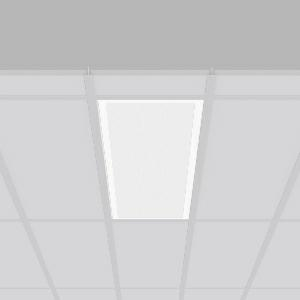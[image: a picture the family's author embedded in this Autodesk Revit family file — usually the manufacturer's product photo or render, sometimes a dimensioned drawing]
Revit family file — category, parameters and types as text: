
# Revit family: sidelite_eco_672373_002_1_71a3
name_source: partatom
category: Lighting Fixtures
units: mm (PartAtom-declared; Revit-internal decimal feet)

## family parameters
Cut with Voids When Loaded = No
Host = Face
Light Source = No
Part Type = Normal
Room Calculation Point = No
Round Connector Dimension = Use Diameter
Shared = No

## types (1)
- SIDELITE ECO (1 x LED Modul 840, 3500 lm, 4000)
    Apparent Load = 29 VA
    CIE Flux Codes = 59 87 97 100 100
    Color Rendering = 80
    Color Temperature = 4000
    Default Elevation = 1800 mm
    Description = Series: SIDELITE ECO
Highly economical recessed luminaire with progressive LED technology. For escape route illumination. Frame made of aluminium, powder-coated. Diffuser plastic microprismatic. Lightguide and diffuser made of non-yellowing plastic (PMMA). Lateral light emission (RZB SIDELITE technology) for homogeneous light distribution. External driver. Second cable inlet for loop through. External driver with simple plug-in locking system. Extended connection cable (1.90 m). Suitable for connection to central battery systems. 
Colour: white
Length: 1245 mm
Width: 308 mm
Cut-out length: 1220 mm
Cut-out width: 285 mm
Recess height: 160 mm
Luminaire: recess height: 40 mm
Weight: 3.64 kg
Operating mode: maintained power mode
Lamp: LED
Socket: without socket
Colour temperature: 4000K
Colour rendering index (CRI): 80
System power: 29 W
Rated luminous flux: 3500 lm
Luminous flux, emergency: 3500 lm
System power, emergency: 29 W
Control gear: Regulated power supply
Protection class: II
Type of protection: IP 20
    Height = 0 mm  [stored 0 ft]
    Lamp = 1 x LED Modul 840
    Lamp Light Flux = 3500 lm
    Lamp count = 1
    Length = 1245 mm
    Lifetime = 50000 h
    Luminous efficacy = 121 lm/W
    Manufacturer = RZB
    ModVariant = No
    Model = 672373.002.1
    Mounting Place = Ceiling
    Mounting Type = Recessed
    Number of Poles = 1
    OnlyDefault = Yes
    Power Factor = 1
    Product Name = SIDELITE ECO
    Product group = Recessed modular luminaires
    ProductGroupID = 406
    Protection Class = Protection class II
    Protection Degree = IP 20
    RLX_Detail_Level = 1
    RLX_Emergency_Light_Flux = 3500 lm
    RLX_Emergency_Type = 3
    RLX_Emergency_Type_DB = Yes
    RlxData = <blob elided: 34385 chars, md5=f166970a>
    Socket = socket
    Standby Power = 0 W
    System Light Flux = 3500 lm
    System Power = 29 W
    Type Comments = Product without accessories
    Type Image = 312368.002.jpg
    URL = http://relux.com
    VarID = ---
    Voltage = 230 V
    Voltage Range = 220-240 V
    Weight = 0.00 kg
    Width = 308 mm

note: [stored X ft] marks values corroborated as IEEE doubles in the binary element streams (Revit-internal decimal feet)

## geometry (parser evidence)
native form markers: Blend x4, Sweep x12
no freeform markers — native parametric forms only
